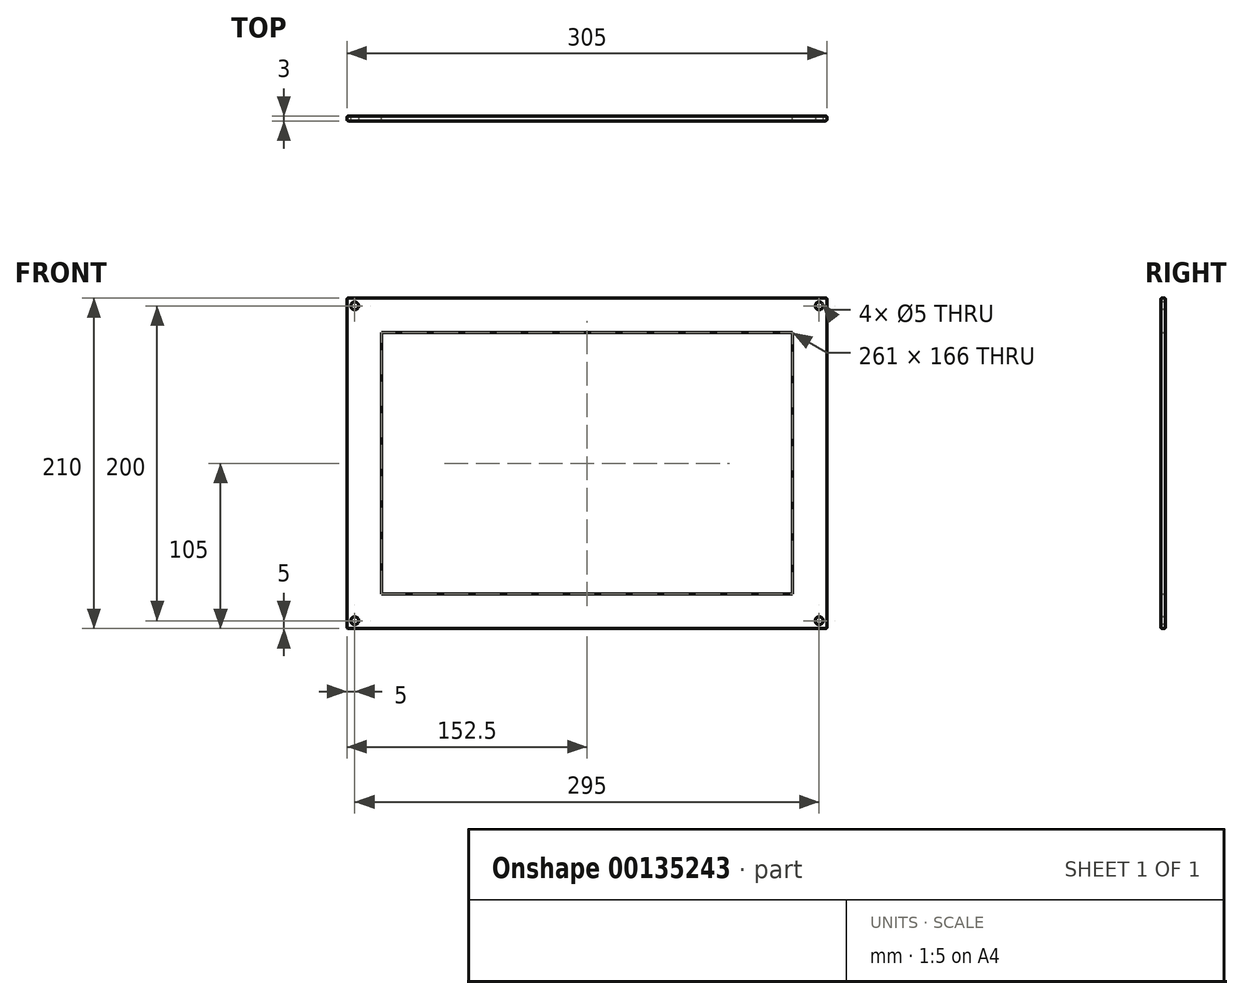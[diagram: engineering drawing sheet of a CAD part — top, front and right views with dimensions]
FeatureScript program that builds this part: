
annotation { "Feature Type Name" : "Feature", "Feature Type Description" : "" }
export const myFeature = defineFeature(function(context is Context, id is Id, definition is map)
    precondition{}
    {
        {
            var Q0;
            Q0=qCreatedBy(makeId("Front.planeOp"),FACE);
            var sketch = newSketch(context, id + "F0", { "sketchPlane" : qUnion([Q0])});
            skLineSegment(sketch, "E0.bottom", {"start": v(152.5, -105) * mm, "end": v(-152.5, -105) * mm});
            skLineSegment(sketch, "E0.top", {"start": v(152.5, 105) * mm, "end": v(-152.5, 105) * mm});
            skLineSegment(sketch, "E0.left", {"start": v(152.5, -105) * mm, "end": v(152.5, 105) * mm});
            skLineSegment(sketch, "E0.right", {"start": v(-152.5, -105) * mm, "end": v(-152.5, 105) * mm});
            skPoint(sketch, "E0.middle", {"position": v(0, 0) * mm});
            skLineSegment(sketch, "E1.bottom", {"start": v(130.5, -83) * mm, "end": v(-130.5, -83) * mm});
            skLineSegment(sketch, "E1.top", {"start": v(130.5, 83) * mm, "end": v(-130.5, 83) * mm});
            skLineSegment(sketch, "E1.left", {"start": v(130.5, -83) * mm, "end": v(130.5, 83) * mm});
            skLineSegment(sketch, "E1.right", {"start": v(-130.5, -83) * mm, "end": v(-130.5, 83) * mm});
            skSolve(sketch);
        }
        {
            var Q0;
            Q0=makeQuery(id+"F0.imprint","IMPRINT",FACE,{"disambiguationData":[TD([[makeQuery(id+"F0.imprint","IMPRINT",EDGE,{"derivedFrom":sQuery(id+"F0.wireOp",EDGE,"E0.bottom")}),-1.0]])]});
            extrude(context, id + "F1", {"entities" : qUnion([Q0]), "depth" : 3 * mm});
        }
        {
            var Q0;
            Q0=makeQuery(id+"F1.opExtrude","SWEPT_EDGE",EDGE,{"disambiguationData":[OSD([sQuery(id+"F0.wireOp",EDGE,"E0.top"),sQuery(id+"F0.wireOp",EDGE,"E0.right")])]});
            var Q1;
            Q1=makeQuery(id+"F1.opExtrude","SWEPT_EDGE",EDGE,{"disambiguationData":[OSD([sQuery(id+"F0.wireOp",EDGE,"E0.bottom"),sQuery(id+"F0.wireOp",EDGE,"E0.right")])]});
            var Q2;
            Q2=makeQuery(id+"F1.opExtrude","SWEPT_EDGE",EDGE,{"disambiguationData":[OSD([sQuery(id+"F0.wireOp",EDGE,"E0.bottom"),sQuery(id+"F0.wireOp",EDGE,"E0.left")])]});
            var Q3;
            Q3=makeQuery(id+"F1.opExtrude","SWEPT_EDGE",EDGE,{"disambiguationData":[OSD([sQuery(id+"F0.wireOp",EDGE,"E0.top"),sQuery(id+"F0.wireOp",EDGE,"E0.left")])]});
            fillet(context, id + "F2", {"entities" : qUnion([Q0, Q1, Q2, Q3]), "radius" : 1 * mm, "tangentPropagation" : true, "allowEdgeOverflow" : false});
        }
        {
            var Q0;
            Q0=makeQuery(id+"F1.opExtrude","CAP_EDGE",EDGE,{"disambiguationData":[OSD([sQuery(id+"F0.wireOp",EDGE,"E0.bottom")])],"isStart":false});
            var Q1;
            Q1=makeQuery(id+"F1.opExtrude","CAP_EDGE",EDGE,{"disambiguationData":[OSD([sQuery(id+"F0.wireOp",EDGE,"E0.bottom")])],"isStart":true});
            fillet(context, id + "F3", {"entities" : qUnion([Q0, Q1]), "radius" : 1 * mm, "tangentPropagation" : true, "allowEdgeOverflow" : false});
        }
        {
            var Q0;
            Q0=makeQuery(id+"F1.opExtrude","CAP_FACE",FACE,{"disambiguationData":[OSD([sQuery(id+"F0.wireOp",EDGE,"E0.bottom"),sQuery(id+"F0.wireOp",EDGE,"E0.top"),sQuery(id+"F0.wireOp",EDGE,"E0.left"),sQuery(id+"F0.wireOp",EDGE,"E0.right"),sQuery(id+"F0.wireOp",EDGE,"E1.bottom"),sQuery(id+"F0.wireOp",EDGE,"E1.top"),sQuery(id+"F0.wireOp",EDGE,"E1.left"),sQuery(id+"F0.wireOp",EDGE,"E1.right")])],"isStart":false});
            var sketch = newSketch(context, id + "F4", { "sketchPlane" : qUnion([Q0])});
            skCircle(sketch, "E2", {"center": v(-147.5, 100) * mm, "radius": 2.5 * mm});
            skCircle(sketch, "E3", {"center": v(147.5, 100) * mm, "radius": 2.5 * mm});
            skCircle(sketch, "E4", {"center": v(147.5, -100) * mm, "radius": 2.5 * mm});
            skCircle(sketch, "E5", {"center": v(-147.5, -100) * mm, "radius": 2.5 * mm});
            skSolve(sketch);
        }
        {
            var Q0;
            Q0 = qSketchRegion(id + "F4", true);
            extrude(context, id + "F5", {"entities" : qUnion([Q0]), "operationType" : NewBodyOperationType.REMOVE, "endBound" : BoundingType.UP_TO_NEXT, "oppositeDirection" : true, "depth" : 25 * mm});
        }
    });
